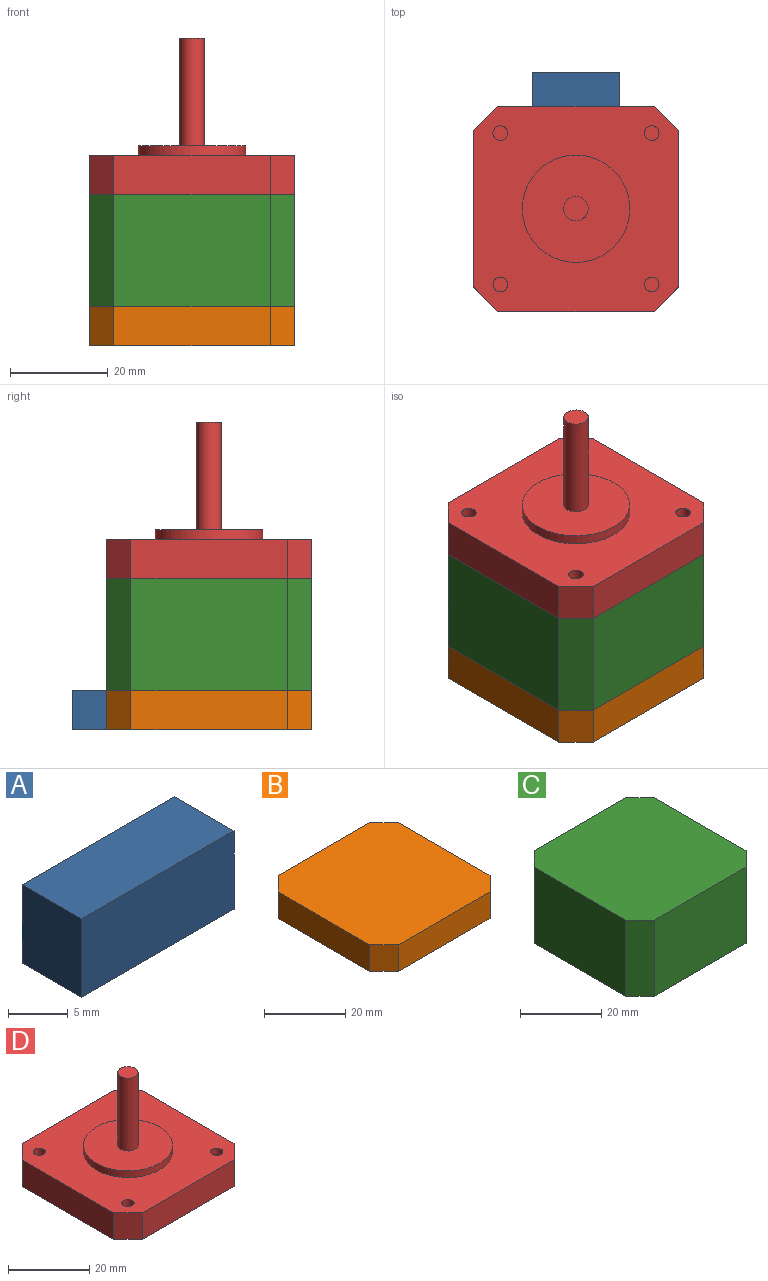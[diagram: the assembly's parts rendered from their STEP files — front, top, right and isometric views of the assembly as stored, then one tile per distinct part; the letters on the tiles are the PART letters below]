
ASSEMBLY  parts=4 mates=3
PART A: 6 faces, bbox 18x7x8 mm
  f0: plane 8x7mm, normal (1,0,0), area 56mm2, adj f1,f3,f4,f5
  f1: plane 18x7mm, normal (0,0,-1), area 126mm2, adj f0,f2,f4,f5
  f2: plane 8x7mm, normal (-1,0,0), area 56mm2, adj f1,f3,f4,f5
  f3: plane 18x7mm, normal (0,0,1), area 126mm2, adj f0,f2,f4,f5
  f4: plane 18x8mm, normal (0,1,0), area 144mm2, adj f0,f1,f2,f3
  f5: plane 18x8mm, normal (0,-1,0), area 144mm2, adj f0,f1,f2,f3
PART B: 10 faces, bbox 42x42x8 mm
  f0: plane 32x8mm, normal (0,1,0), area 256mm2, adj f4,f5,f6,f8
  f1: plane 32x8mm, normal (-1,0,0), area 256mm2, adj f4,f5,f6,f7
  f2: plane 32x8mm, normal (0,-1,0), area 256mm2, adj f4,f5,f7,f9
  f3: plane 32x8mm, normal (1,0,0), area 256mm2, adj f4,f5,f8,f9
  f4: plane 42x42mm, normal (0,0,1), area 1714mm2, adj f0,f1,f2,f3,f6,f7,f8,f9
  f5: plane 42x42mm, normal (0,0,-1), area 1714mm2, adj f0,f1,f2,f3,f6,f7,f8,f9
  f6: plane 8x5mm, normal (-0.71,0.71,0), area 56.6mm2, adj f0,f1,f4,f5
  f7: plane 8x5mm, normal (-0.71,-0.71,0), area 56.6mm2, adj f1,f2,f4,f5
  f8: plane 8x5mm, normal (0.71,0.71,0), area 56.6mm2, adj f0,f3,f4,f5
  f9: plane 8x5mm, normal (0.71,-0.71,0), area 56.6mm2, adj f2,f3,f4,f5
PART C: 10 faces, bbox 42x42x23 mm
  f0: plane 32x23mm, normal (0,1,0), area 736mm2, adj f4,f5,f6,f9
  f1: plane 32x23mm, normal (-1,0,0), area 736mm2, adj f4,f5,f6,f7
  f2: plane 32x23mm, normal (0,-1,0), area 736mm2, adj f4,f5,f7,f8
  f3: plane 32x23mm, normal (1,0,0), area 736mm2, adj f4,f5,f8,f9
  f4: plane 42x42mm, normal (0,0,1), area 1714mm2, adj f0,f1,f2,f3,f6,f7,f8,f9
  f5: plane 42x42mm, normal (0,0,-1), area 1714mm2, adj f0,f1,f2,f3,f6,f7,f8,f9
  f6: plane 23x5mm, normal (-0.71,0.71,0), area 162.6mm2, adj f0,f1,f4,f5
  f7: plane 23x5mm, normal (-0.71,-0.71,0), area 162.6mm2, adj f1,f2,f4,f5
  f8: plane 23x5mm, normal (0.71,-0.71,0), area 162.6mm2, adj f2,f3,f4,f5
  f9: plane 23x5mm, normal (0.71,0.71,0), area 162.6mm2, adj f0,f3,f4,f5
PART D: 22 faces, bbox 42x42x32 mm
  f0: plane 32x8mm, normal (0,1,0), area 256mm2, adj f4,f5,f6,f9
  f1: plane 32x8mm, normal (-1,0,0), area 256mm2, adj f4,f5,f6,f7
  f2: plane 32x8mm, normal (0,-1,0), area 256mm2, adj f4,f5,f7,f8
  f3: plane 32x8mm, normal (1,0,0), area 256mm2, adj f4,f5,f8,f9
  f4: plane 42x42mm, normal (0,0,1), area 1305.6mm2, adj f0,f1,f2,f3,f6,f7,f8,f9
  f5: plane 42x42mm, normal (0,0,-1), area 1714mm2, adj f0,f1,f2,f3,f6,f7,f8,f9
  f6: plane 8x5mm, normal (-0.71,0.71,0), area 56.6mm2, adj f0,f1,f4,f5
  f7: plane 8x5mm, normal (-0.71,-0.71,0), area 56.6mm2, adj f1,f2,f4,f5
  f8: plane 8x5mm, normal (0.71,-0.71,0), area 56.6mm2, adj f2,f3,f4,f5
  f9: plane 8x5mm, normal (0.71,0.71,0), area 56.6mm2, adj f0,f3,f4,f5
  f10: cylinder r=11mm len=22mm, axis (0,0,-1), area 138.2mm2, adj f4,f11
  f11: plane 22x22mm, normal (0,0,1), area 360.5mm2, adj f10,f13
  f12: plane 5x5mm, normal (0,0,1), area 19.6mm2, adj f13
  f13: cylinder r=2.5mm len=22mm, axis (0,0,-1), area 345.6mm2, adj f11,f12
  f14: cylinder r=1.5mm len=5mm, axis (0,0,1), area 47.1mm2, adj f4,f15
  f15: plane 3x3mm, normal (0,0,1), area 7.1mm2, adj f14
  f16: cylinder r=1.5mm len=5mm, axis (0,0,1), area 47.1mm2, adj f4,f17
  f17: plane 3x3mm, normal (0,0,1), area 7.1mm2, adj f16
  f18: cylinder r=1.5mm len=5mm, axis (0,0,1), area 47.1mm2, adj f4,f19
  f19: plane 3x3mm, normal (0,0,1), area 7.1mm2, adj f18
  f20: cylinder r=1.5mm len=5mm, axis (0,0,1), area 47.1mm2, adj f4,f21
  f21: plane 3x3mm, normal (0,0,1), area 7.1mm2, adj f20
PLACE A t=(0,33,0)mm
PLACE B t=(0,33,0)mm
PLACE C t=(0,33,0)mm
PLACE D t=(0,33,0)mm
MATE fastened C.f5 <-> B.f4  axis (0,0,-1) through (0,33,8)mm
MATE fastened C.f4 <-> D.f13  axis (0,0,1) through (0,33,31)mm
MATE fastened B.f0 <-> A.f5  axis (0,1,0) through (0,54,0)mm
